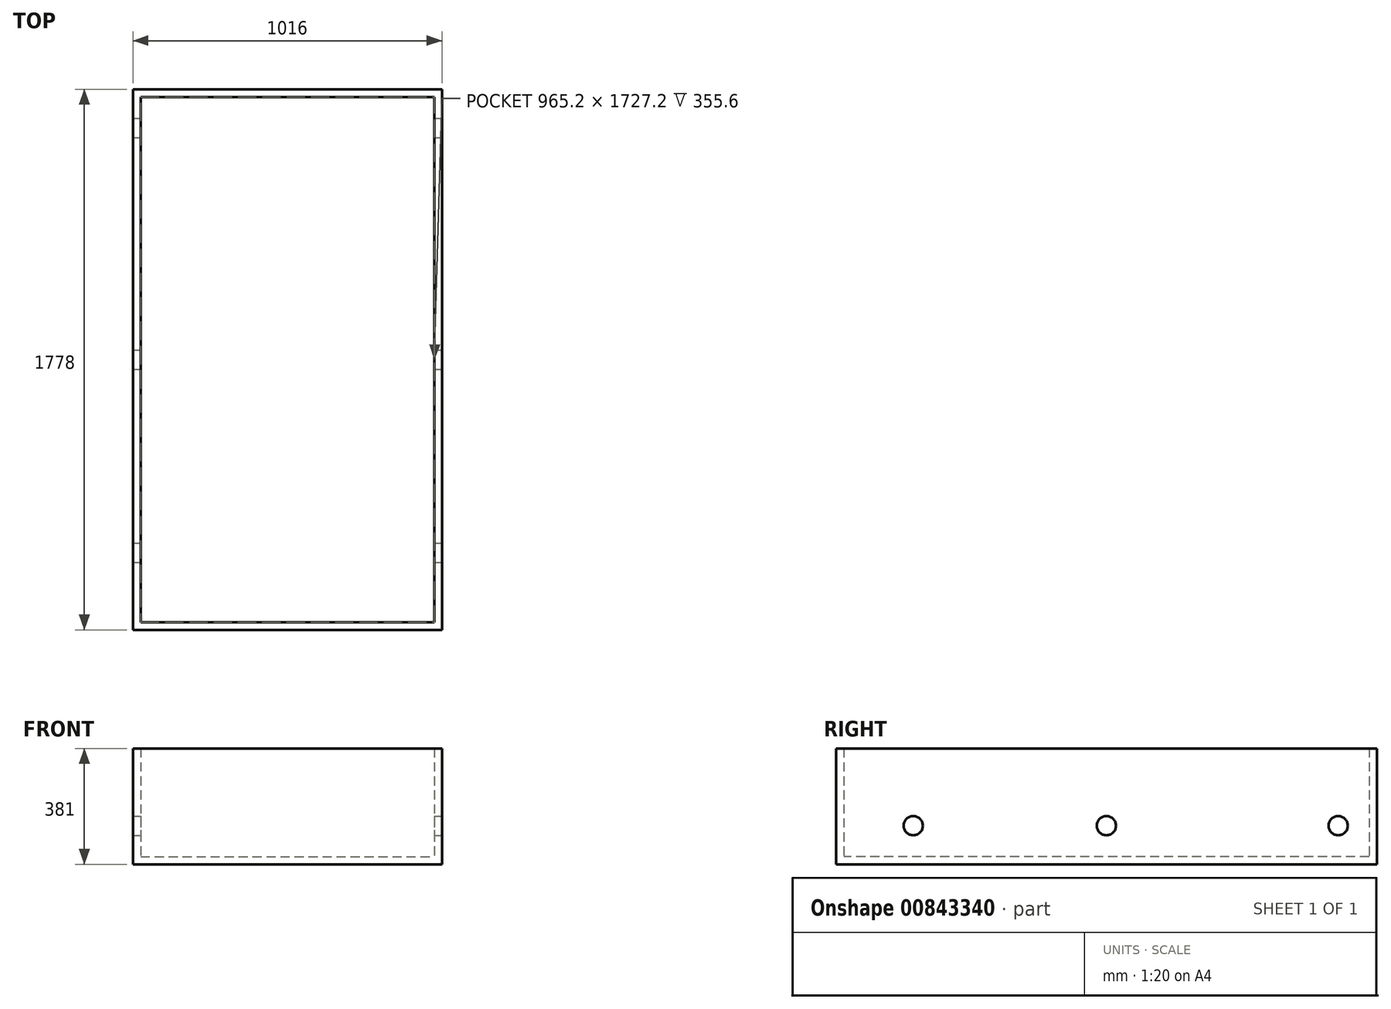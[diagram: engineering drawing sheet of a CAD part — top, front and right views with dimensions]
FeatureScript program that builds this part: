
annotation { "Feature Type Name" : "Feature", "Feature Type Description" : "" }
export const myFeature = defineFeature(function(context is Context, id is Id, definition is map)
    precondition{}
    {
        {
            var Q0;
            Q0=qCreatedBy(makeId("Front.planeOp"),FACE);
            var sketch = newSketch(context, id + "F0", { "sketchPlane" : qUnion([Q0])});
            skLineSegment(sketch, "E0.bottom", {"start": v(-508, 381) * mm, "end": v(508, 381) * mm});
            skLineSegment(sketch, "E0.top", {"start": v(-508, 0) * mm, "end": v(508, 0) * mm});
            skLineSegment(sketch, "E0.left", {"start": v(-508, 381) * mm, "end": v(-508, 0) * mm});
            skLineSegment(sketch, "E0.right", {"start": v(508, 381) * mm, "end": v(508, 0) * mm});
            skSolve(sketch);
        }
        {
            var Q0;
            Q0=makeQuery(id+"F0.imprint","IMPRINT",FACE,{"disambiguationData":[TD([[makeQuery(id+"F0.imprint","IMPRINT",EDGE,{"derivedFrom":sQuery(id+"F0.wireOp",EDGE,"E0.bottom")}),-1.0]])]});
            extrude(context, id + "F1", {"entities" : qUnion([Q0]), "oppositeDirection" : true, "depth" : 1778 * mm, "offsetDistance" : 25.4 * mm});
        }
        {
            var Q0;
            Q0=makeQuery(id+"F1.opExtrude","SWEPT_FACE",FACE,{"disambiguationData":[OSD([sQuery(id+"F0.wireOp",EDGE,"E0.bottom")])]});
            shell(context, id + "F2", {"entities" : qUnion([Q0]), "thickness" : 25.4 * mm});
        }
        {
            var Q0;
            Q0=makeQuery(id+"F1.opExtrude","SWEPT_FACE",FACE,{"disambiguationData":[OSD([sQuery(id+"F0.wireOp",EDGE,"E0.right")])]});
            var sketch = newSketch(context, id + "F3", { "sketchPlane" : qUnion([Q0])});
            skCircle(sketch, "E1", {"center": v(254, 127) * mm, "radius": 31.75 * mm});
            skCircle(sketch, "E2", {"center": v(1651, 127) * mm, "radius": 31.75 * mm});
            skCircle(sketch, "E3", {"center": v(889, 127) * mm, "radius": 31.75 * mm});
            skSolve(sketch);
        }
        {
            var Q0;
            Q0=makeQuery(id+"F3.imprint","IMPRINT",FACE,{"disambiguationData":[TD([[makeQuery(id+"F3.imprint","IMPRINT",EDGE,{"derivedFrom":sQuery(id+"F3.wireOp",EDGE,"E1")}),1.0]])]});
            var Q1;
            Q1=makeQuery(id+"F3.imprint","IMPRINT",FACE,{"disambiguationData":[TD([[makeQuery(id+"F3.imprint","IMPRINT",EDGE,{"derivedFrom":sQuery(id+"F3.wireOp",EDGE,"E2")}),1.0]])]});
            var Q2;
            Q2=makeQuery(id+"F3.imprint","IMPRINT",FACE,{"disambiguationData":[TD([[makeQuery(id+"F3.imprint","IMPRINT",EDGE,{"derivedFrom":sQuery(id+"F3.wireOp",EDGE,"E3")}),1.0]])]});
            extrude(context, id + "F4", {"entities" : qUnion([Q0, Q1, Q2]), "operationType" : NewBodyOperationType.REMOVE, "endBound" : BoundingType.THROUGH_ALL, "oppositeDirection" : true, "depth" : 25.4 * mm, "offsetDistance" : 25.4 * mm});
        }
    });
